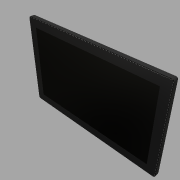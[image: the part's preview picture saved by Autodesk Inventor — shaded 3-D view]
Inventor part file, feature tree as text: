
AUTODESK INVENTOR PART (.ipt)
format: ipt  version: 2019 (Build 230136000, 136)  size: 342,016 bytes
history: native  units: mm
features: extrude x7, sketch x6, other x6, fillet x3, chamfer x2, projected_geometry x2, plane x1
ambient origin geometry x8: Origin, YZ Plane, XZ Plane, XY Plane, X Axis, Y Axis, Z Axis, Center Point
bodies: Solid1 (feature_tree), Solid2 (feature_tree), Solid3 (feature_tree), Solid4 (feature_tree), Solid5 (feature_tree)
feature tree (27):
  extrude  "Extrusion1"  Depth=187.5mm
  fillet  "Fillet1"  Radius=10.5mm
  chamfer  "Chamfer1"  Distance=1.0mm Angle=45.0deg
  chamfer  "Chamfer2"  Distance=1.5mm Angle=45.0deg
  extrude  "Extrusion2"  Depth=0.25mm TaperAngle=0.0deg
  fillet  "Fillet2"  Radius=0.25mm
  plane  "Work Plane1"
  extrude  "Extrusion3"  Depth=17.0mm
  extrude  "Extrusion4"  Depth=1.0mm TaperAngle=0.0deg
  sketch  "Sketch5"  dims[d17=1.0mm d18=0.0mm d19=1.0mm d20=0.0mm]
  extrude  "Extrusion5"  Depth=5.0mm
  extrude  "Extrusion6"  Depth=1.0mm
  fillet  "Fillet3"  Radius=1.0mm
  extrude  "Extrusion7"  TaperAngle=0.0deg  [1 undecoded]
  other  "USB Micro Center"
  sketch  "Sketch1"  dims[d0=305.0mm d1=187.5mm d2=10.5mm d3=0.0mm]
  sketch  "Sketch2"  dims[d4=4.0mm d5=0.5mm d6=1.0mm d7=45.0deg d8=0.5mm d9=1.5mm d10=45.0deg]
  projected_geometry  "Projected Loop1"
  sketch  "Sketch3"  dims[d11=0.5mm d12=0.25mm d13=0.0mm d14=0.25mm]
  projected_geometry  "Projected Loop2"
  sketch  "Sketch4"  dims[d15=0.25mm d16=17.0mm]
  sketch  "Sketch6"  dims[d21=3.5mm d22=5.0mm d23=15.0mm d24=1.0mm d25=0.0mm d26=2.65mm d27=8.34mm d28=15.0mm d29=0.75mm d30=0.7mm d31=6.0mm d32=0.0mm d45=1.5mm d46=10.6mm d47=1.0mm d48=8.1mm d50=1.0mm d51=1.0mm d52=1.0mm d53=1.0mm d54=1.25mm d55=1.5mm d56=20.0mm d58=0.0mm d59=1.85mm d60=6.9mm d61=20.0mm d62=0.0mm d63=0.7mm d64=0.7mm d65=0.7mm d66=0.7mm d67=5.0mm d68=0.0mm d69=0.5mm d70=0.0mm d71=6.35mm d72=19.175mm d73=8.675mm d74=40.0mm d76=7.85mm d77=10.0mm d79=10.0mm d81=6.35mm d82=0.0mm d83=9.35mm d84=1.0mm d85=0.0mm]
  other  "Work Point1"
  other  "USB C Center"
  other  "Work Point2"
  other  "HDMI Mini Center"
  other  "Work Point3"
note: 1 required parameter value undecoded (feature->parameter linkage not recoverable at this tier; creation-order binding heuristic only, values carry confidence <= 0.55)
